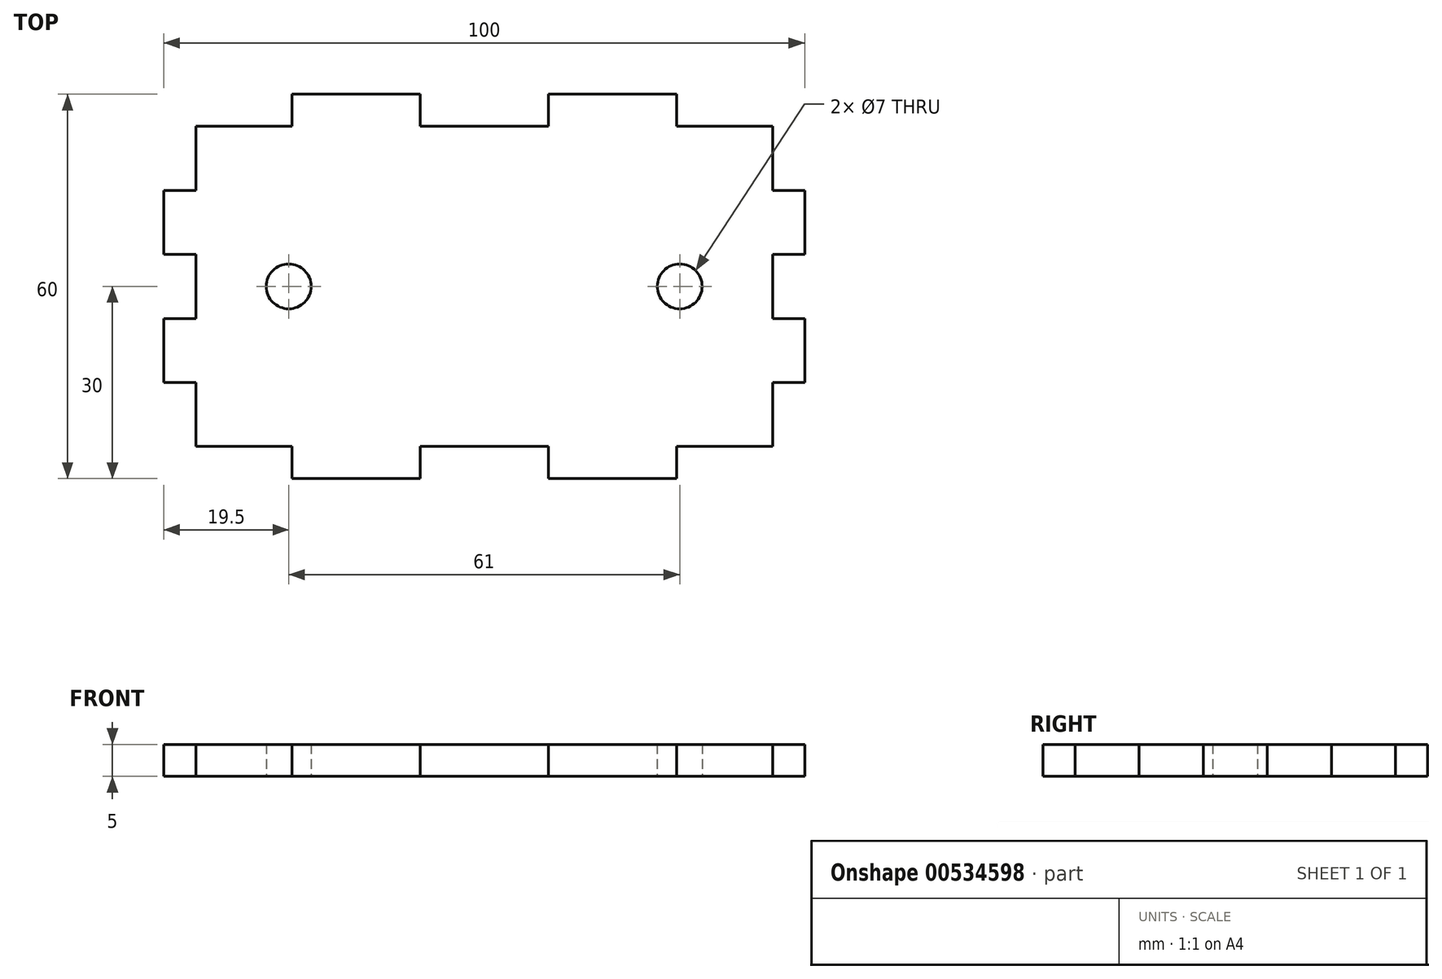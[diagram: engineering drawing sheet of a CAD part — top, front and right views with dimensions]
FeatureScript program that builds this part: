
annotation { "Feature Type Name" : "Feature", "Feature Type Description" : "" }
export const myFeature = defineFeature(function(context is Context, id is Id, definition is map)
    precondition{}
    {
        {
            var Q0;
            Q0=qCreatedBy(makeId("Top.planeOp"),FACE);
            var sketch = newSketch(context, id + "F0", { "sketchPlane" : qUnion([Q0])});
            skLineSegment(sketch, "E0.bottom", {"start": v(45, 25) * mm, "end": v(30, 25) * mm});
            skLineSegment(sketch, "E0.top", {"start": v(45, -25) * mm, "end": v(30, -25) * mm});
            skLineSegment(sketch, "E0.left", {"start": v(45, 25) * mm, "end": v(45, 15) * mm});
            skLineSegment(sketch, "E0.right", {"start": v(-45, 25) * mm, "end": v(-45, 15) * mm});
            skPoint(sketch, "E0.middle", {"position": v(0, 0) * mm});
            skLineSegment(sketch, "E1.bottom", {"start": v(-50, 30) * mm, "end": v(50, 30) * mm, "construction": true});
            skLineSegment(sketch, "E1.top", {"start": v(-50, -30) * mm, "end": v(50, -30) * mm, "construction": true});
            skLineSegment(sketch, "E1.left", {"start": v(-50, 30) * mm, "end": v(-50, -30) * mm, "construction": true});
            skLineSegment(sketch, "E1.right", {"start": v(50, 30) * mm, "end": v(50, -30) * mm, "construction": true});
            skLineSegment(sketch, "E2.bottom", {"start": v(-45, 15) * mm, "end": v(-50, 15) * mm});
            skLineSegment(sketch, "E2.top", {"start": v(-45, 5) * mm, "end": v(-50, 5) * mm});
            skLineSegment(sketch, "E2.right", {"start": v(-50, 15) * mm, "end": v(-50, 5) * mm});
            skLineSegment(sketch, "E3.bottom", {"start": v(-45, -15) * mm, "end": v(-50, -15) * mm});
            skLineSegment(sketch, "E3.top", {"start": v(-45, -5) * mm, "end": v(-50, -5) * mm});
            skLineSegment(sketch, "E3.right", {"start": v(-50, -15) * mm, "end": v(-50, -5) * mm});
            skLineSegment(sketch, "E4.MirrorCS", {"start": v(45, 15) * mm, "end": v(50, 15) * mm});
            skLineSegment(sketch, "E5.MirrorCS", {"start": v(45, 5) * mm, "end": v(50, 5) * mm});
            skLineSegment(sketch, "E6.MirrorCS", {"start": v(45, -5) * mm, "end": v(50, -5) * mm});
            skLineSegment(sketch, "E7.MirrorCS", {"start": v(45, -15) * mm, "end": v(50, -15) * mm});
            skLineSegment(sketch, "E8", {"start": v(50, 15) * mm, "end": v(50, 5) * mm});
            skLineSegment(sketch, "E9", {"start": v(50, -5) * mm, "end": v(50, -15) * mm});
            skLineSegment(sketch, "E10.trimOffspring", {"start": v(-45, 5) * mm, "end": v(-45, -5) * mm});
            skLineSegment(sketch, "E11.trimOffspring", {"start": v(-45, -15) * mm, "end": v(-45, -25) * mm});
            skLineSegment(sketch, "E12.trimOffspring", {"start": v(45, 5) * mm, "end": v(45, -5) * mm});
            skLineSegment(sketch, "E13.trimOffspring", {"start": v(45, -15) * mm, "end": v(45, -25) * mm});
            skLineSegment(sketch, "E14.top", {"start": v(-30, 30) * mm, "end": v(-10, 30) * mm});
            skLineSegment(sketch, "E14.left", {"start": v(-30, 25) * mm, "end": v(-30, 30) * mm});
            skLineSegment(sketch, "E14.right", {"start": v(-10, 25) * mm, "end": v(-10, 30) * mm});
            skLineSegment(sketch, "E15.top", {"start": v(10, 30) * mm, "end": v(30, 30) * mm});
            skLineSegment(sketch, "E15.left", {"start": v(10, 25) * mm, "end": v(10, 30) * mm});
            skLineSegment(sketch, "E15.right", {"start": v(30, 25) * mm, "end": v(30, 30) * mm});
            skLineSegment(sketch, "E16.MirrorCS", {"start": v(-30, -25) * mm, "end": v(-30, -30) * mm});
            skLineSegment(sketch, "E17.MirrorCS", {"start": v(-10, -25) * mm, "end": v(-10, -30) * mm});
            skLineSegment(sketch, "E18.MirrorCS", {"start": v(10, -25) * mm, "end": v(10, -30) * mm});
            skLineSegment(sketch, "E19.MirrorCS", {"start": v(30, -25) * mm, "end": v(30, -30) * mm});
            skLineSegment(sketch, "E20", {"start": v(-30, -30) * mm, "end": v(-10, -30) * mm});
            skLineSegment(sketch, "E21", {"start": v(10, -30) * mm, "end": v(30, -30) * mm});
            skLineSegment(sketch, "E22.trimOffspring", {"start": v(-30, 25) * mm, "end": v(-45, 25) * mm});
            skLineSegment(sketch, "E23.trimOffspring", {"start": v(10, 25) * mm, "end": v(-10, 25) * mm});
            skLineSegment(sketch, "E24.trimOffspring", {"start": v(10, -25) * mm, "end": v(-10, -25) * mm});
            skLineSegment(sketch, "E25.trimOffspring", {"start": v(-30, -25) * mm, "end": v(-45, -25) * mm});
            skCircle(sketch, "E26", {"center": v(-30.5, 0) * mm, "radius": 3.5 * mm});
            skCircle(sketch, "E27", {"center": v(30.5, 0) * mm, "radius": 3.5 * mm});
            skLineSegment(sketch, "E28.bottom", {"start": v(10.5, 13.42) * mm, "end": v(-10.5, 13.42) * mm, "construction": true});
            skLineSegment(sketch, "E28.top", {"start": v(10.5, -13.42) * mm, "end": v(-10.5, -13.42) * mm, "construction": true});
            skLineSegment(sketch, "E28.left", {"start": v(10.5, 13.42) * mm, "end": v(10.5, -13.42) * mm, "construction": true});
            skLineSegment(sketch, "E28.right", {"start": v(-10.5, 13.42) * mm, "end": v(-10.5, -13.42) * mm, "construction": true});
            skSolve(sketch);
        }
        {
            var Q0;
            Q0 = qSketchRegion(id + "F0", true);
            extrude(context, id + "F1", {"entities" : qUnion([Q0]), "depth" : 5 * mm, "offsetDistance" : 25 * mm});
        }
    });
